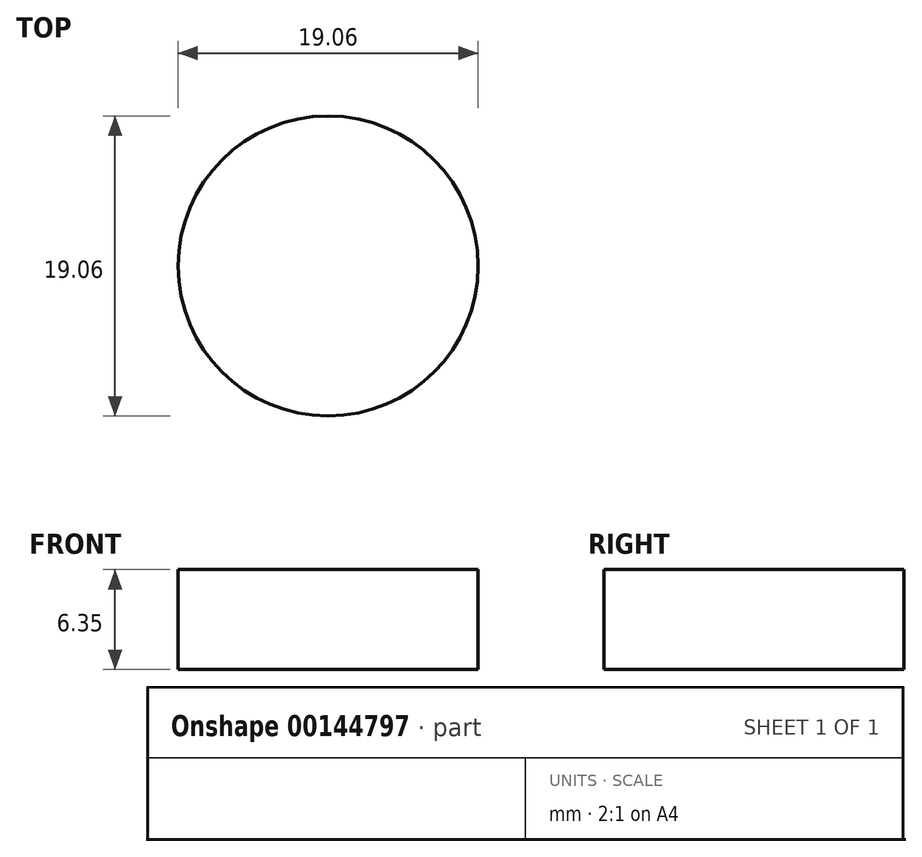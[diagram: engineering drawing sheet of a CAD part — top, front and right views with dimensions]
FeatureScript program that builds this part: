
annotation { "Feature Type Name" : "Feature", "Feature Type Description" : "" }
export const myFeature = defineFeature(function(context is Context, id is Id, definition is map)
    precondition{}
    {
        {
            var Q0;
            Q0=qCreatedBy(makeId("Top.planeOp"),FACE);
            var sketch = newSketch(context, id + "F0", { "sketchPlane" : qUnion([Q0])});
            skCircle(sketch, "E0", {"center": v(0, 0) * mm, "radius": 9.53 * mm});
            skSolve(sketch);
        }
        {
            var Q0;
            Q0=makeQuery(id+"F0.imprint","IMPRINT",FACE,{"disambiguationData":[TD([[makeQuery(id+"F0.imprint","IMPRINT",EDGE,{"derivedFrom":sQuery(id+"F0.wireOp",EDGE,"E0")}),1.0]])]});
            extrude(context, id + "F1", {"entities" : qUnion([Q0]), "depth" : 6.35 * mm});
        }
    });
